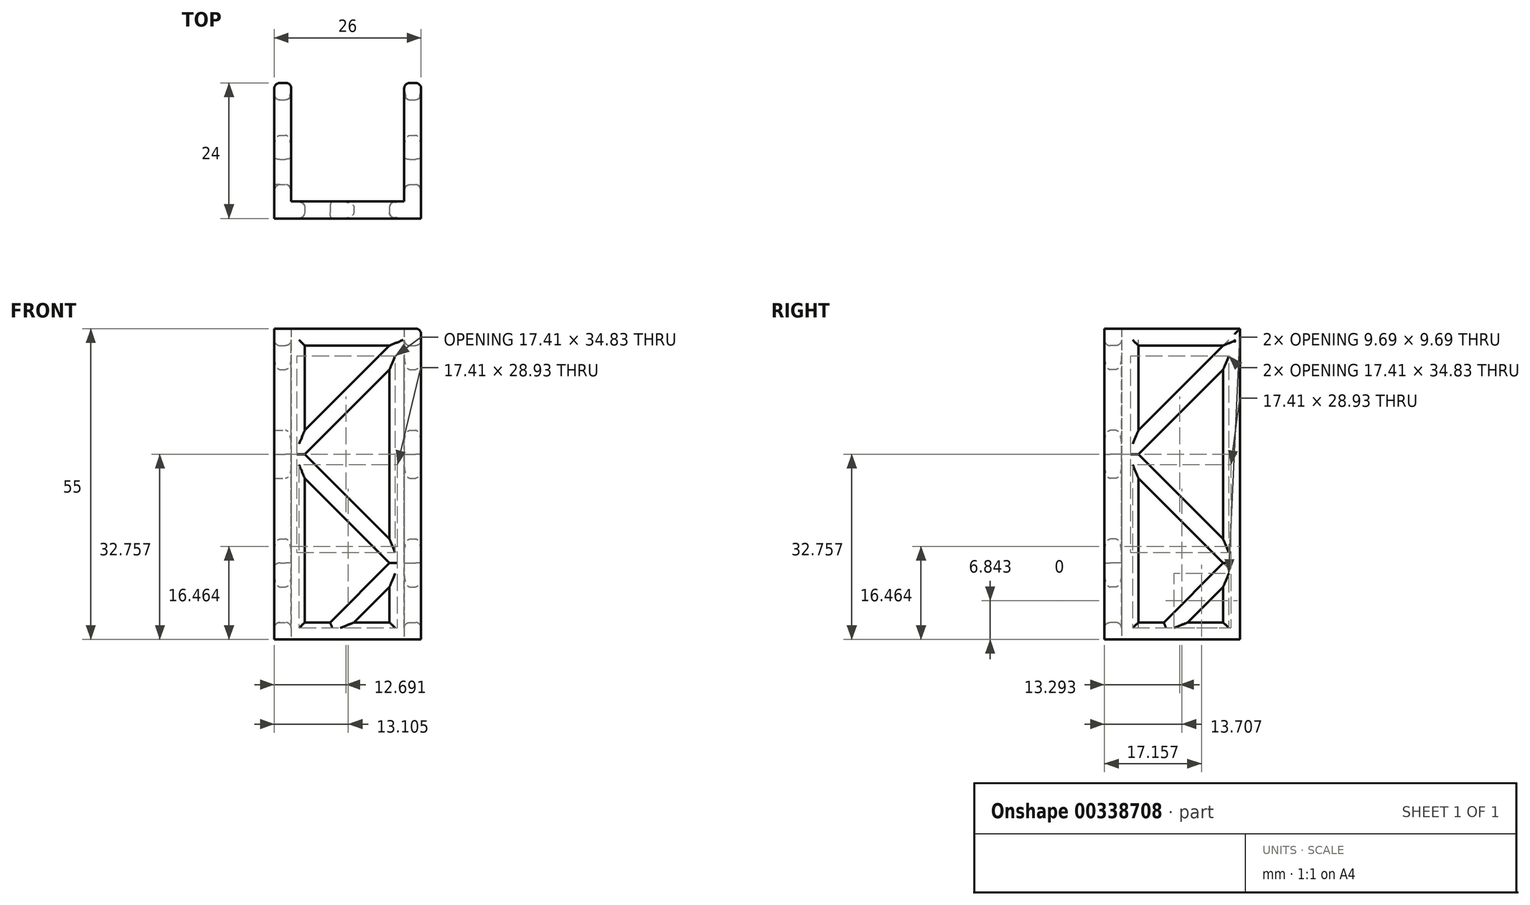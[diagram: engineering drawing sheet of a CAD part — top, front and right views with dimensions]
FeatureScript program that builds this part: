
annotation { "Feature Type Name" : "Feature", "Feature Type Description" : "" }
export const myFeature = defineFeature(function(context is Context, id is Id, definition is map)
    precondition{}
    {
        {
            var Q0;
            Q0=qCreatedBy(makeId("Top.planeOp"),FACE);
            var sketch = newSketch(context, id + "F0", { "sketchPlane" : qUnion([Q0])});
            skLineSegment(sketch, "E0.bottom", {"start": v(-13, 0) * mm, "end": v(-10, 0) * mm});
            skLineSegment(sketch, "E0.top", {"start": v(-13, -24) * mm, "end": v(13, -24) * mm});
            skLineSegment(sketch, "E0.left", {"start": v(-13, 0) * mm, "end": v(-13, -24) * mm});
            skLineSegment(sketch, "E0.right", {"start": v(13, 0) * mm, "end": v(13, -24) * mm});
            skLineSegment(sketch, "E1.top", {"start": v(-10, -21) * mm, "end": v(10, -21) * mm});
            skLineSegment(sketch, "E1.left", {"start": v(-10, 0) * mm, "end": v(-10, -21) * mm});
            skLineSegment(sketch, "E1.right", {"start": v(10, 0) * mm, "end": v(10, -21) * mm});
            skLineSegment(sketch, "E2.trimOffspring", {"start": v(10, 0) * mm, "end": v(13, 0) * mm});
            skSolve(sketch);
        }
        {
            var Q0;
            Q0 = qSketchRegion(id + "F0", true);
            extrude(context, id + "F1", {"entities" : qUnion([Q0]), "endBound" : BoundingType.SYMMETRIC, "depth" : 55 * mm});
        }
        {
            var Q0;
            Q0=makeQuery(id+"F1.opExtrude","SWEPT_FACE",FACE,{"disambiguationData":[OSD([sQuery(id+"F0.wireOp",EDGE,"E0.right")])]});
            var sketch = newSketch(context, id + "F2", { "sketchPlane" : qUnion([Q0])});
            skLineSegment(sketch, "E3", {"start": v(-3, -24.5) * mm, "end": v(-3, 24.5) * mm});
            skLineSegment(sketch, "E4", {"start": v(-18, -24.5) * mm, "end": v(-18, 24.5) * mm});
            skLineSegment(sketch, "E5", {"start": v(-18, 24.5) * mm, "end": v(-3, 24.5) * mm});
            skLineSegment(sketch, "E6", {"start": v(-3, 24.5) * mm, "end": v(-18, 9.5) * mm});
            skLineSegment(sketch, "E7", {"start": v(-3, 20.26) * mm, "end": v(-18, 5.26) * mm});
            skLineSegment(sketch, "E8", {"start": v(-18, 5.26) * mm, "end": v(-3, -9.74) * mm});
            skLineSegment(sketch, "E9.0", {"start": v(-18, 1.01) * mm, "end": v(-3, -13.99) * mm});
            skLineSegment(sketch, "E10", {"start": v(-18, -24.5) * mm, "end": v(-3, -24.5) * mm});
            skLineSegment(sketch, "E11", {"start": v(-3, -13.99) * mm, "end": v(-13.51, -24.5) * mm});
            skLineSegment(sketch, "E12.0", {"start": v(-3, -18.23) * mm, "end": v(-9.27, -24.5) * mm});
            skPoint(sketch, "E13.start.orphan", {"position": v(0, 47.5) * mm});
            skSolve(sketch);
        }
        {
            var Q0;
            {var subQ0=sQuery(id+"F2.wireOp",EDGE,"E5");Q0=makeQuery(id+"F2.imprint","IMPRINT",FACE,{"disambiguationData":[TD([[makeQuery(id+"F2.imprint","IMPRINT",EDGE,{"derivedFrom":subQ0}),-1.0]])]});}
            var Q1;
            {var subQ0=sQuery(id+"F2.wireOp",EDGE,"E7");Q1=makeQuery(id+"F2.imprint","IMPRINT",FACE,{"disambiguationData":[TD([[makeQuery(id+"F2.imprint","IMPRINT",EDGE,{"derivedFrom":subQ0}),1.0]])]});}
            var Q2;
            {var subQ3=sQuery(id+"F2.wireOp",EDGE,"E9.0");Q2=makeQuery(id+"F2.imprint","IMPRINT",FACE,{"disambiguationData":[TD([[makeQuery(id+"F2.imprint","IMPRINT",EDGE,{"derivedFrom":subQ3}),-1.0]])]});}
            var Q3;
            {var subQ3=sQuery(id+"F2.wireOp",EDGE,"E12.0");Q3=makeQuery(id+"F2.imprint","IMPRINT",FACE,{"disambiguationData":[TD([[makeQuery(id+"F2.imprint","IMPRINT",EDGE,{"derivedFrom":subQ3}),1.0]])]});}
            extrude(context, id + "F3", {"entities" : qUnion([Q0, Q1, Q2, Q3]), "operationType" : NewBodyOperationType.REMOVE, "endBound" : BoundingType.SYMMETRIC, "oppositeDirection" : true, "depth" : 1000 * mm});
        }
        {
            var Q0;
            Q0=qCreatedBy(makeId("Front.planeOp"),FACE);
            var sketch = newSketch(context, id + "F4", { "sketchPlane" : qUnion([Q0])});
            skLineSegment(sketch, "E14", {"start": v(7.4, -24.5) * mm, "end": v(7.4, 24.5) * mm});
            skLineSegment(sketch, "E15", {"start": v(-7.6, -24.5) * mm, "end": v(-7.6, 24.5) * mm});
            skLineSegment(sketch, "E16", {"start": v(-7.6, 24.5) * mm, "end": v(7.4, 24.5) * mm});
            skLineSegment(sketch, "E17", {"start": v(7.4, 24.5) * mm, "end": v(-7.6, 9.5) * mm});
            skLineSegment(sketch, "E18", {"start": v(7.4, 20.26) * mm, "end": v(-7.6, 5.26) * mm});
            skLineSegment(sketch, "E19", {"start": v(-7.6, 5.26) * mm, "end": v(7.4, -9.74) * mm});
            skLineSegment(sketch, "E20.0", {"start": v(-7.6, 1.01) * mm, "end": v(7.4, -13.99) * mm});
            skLineSegment(sketch, "E21", {"start": v(-7.6, -24.5) * mm, "end": v(7.4, -24.5) * mm});
            skLineSegment(sketch, "E22", {"start": v(7.4, -13.99) * mm, "end": v(-3.12, -24.5) * mm});
            skLineSegment(sketch, "E23.0", {"start": v(7.4, -18.23) * mm, "end": v(1.13, -24.5) * mm});
            skSolve(sketch);
        }
        {
            var Q0;
            {var subQ3=sQuery(id+"F4.wireOp",EDGE,"E23.0");Q0=makeQuery(id+"F4.imprint","IMPRINT",FACE,{"disambiguationData":[TD([[makeQuery(id+"F4.imprint","IMPRINT",EDGE,{"derivedFrom":subQ3}),1.0]])]});}
            var Q1;
            {var subQ3=sQuery(id+"F4.wireOp",EDGE,"E20.0");Q1=makeQuery(id+"F4.imprint","IMPRINT",FACE,{"disambiguationData":[TD([[makeQuery(id+"F4.imprint","IMPRINT",EDGE,{"derivedFrom":subQ3}),-1.0]])]});}
            var Q2;
            {var subQ0=sQuery(id+"F4.wireOp",EDGE,"E18");Q2=makeQuery(id+"F4.imprint","IMPRINT",FACE,{"disambiguationData":[TD([[makeQuery(id+"F4.imprint","IMPRINT",EDGE,{"derivedFrom":subQ0}),1.0]])]});}
            var Q3;
            {var subQ0=sQuery(id+"F4.wireOp",EDGE,"E16");Q3=makeQuery(id+"F4.imprint","IMPRINT",FACE,{"disambiguationData":[TD([[makeQuery(id+"F4.imprint","IMPRINT",EDGE,{"derivedFrom":subQ0}),-1.0]])]});}
            extrude(context, id + "F5", {"entities" : qUnion([Q0, Q1, Q2, Q3]), "operationType" : NewBodyOperationType.REMOVE, "endBound" : BoundingType.SYMMETRIC, "oppositeDirection" : true, "depth" : 1000 * mm});
        }
        {
            var Q0;
            Q0=makeQuery(id+"F1.opExtrude","SWEPT_EDGE",EDGE,{"disambiguationData":[OSD([sQuery(id+"F0.wireOp",EDGE,"E1.right"),sQuery(id+"F0.wireOp",EDGE,"E2.trimOffspring")])]});
            var Q1;
            Q1=makeQuery(id+"F3.boolean.opBoolean","INTERSECT",EDGE,{"derivedFrom":[makeQuery(id+"F1.opExtrude","SWEPT_FACE",FACE,{"disambiguationData":[OSD([sQuery(id+"F0.wireOp",EDGE,"E0.right")])]}),makeQuery(id+"F3.opExtrude","SWEPT_FACE",FACE,{"disambiguationData":[OSD([sQuery(id+"F2.wireOp",EDGE,"E7")])]})]});
            var Q2;
            {var subQ0=sQuery(id+"F2.wireOp",EDGE,"E3");Q2=makeQuery(id+"F3.boolean.opBoolean","INTERSECT",EDGE,{"derivedFrom":[makeQuery(id+"F1.opExtrude","SWEPT_FACE",FACE,{"disambiguationData":[OSD([sQuery(id+"F0.wireOp",EDGE,"E0.right")])]}),makeQuery(id+"F3.opExtrude","SWEPT_FACE",FACE,{"disambiguationData":[OSD([subQ0]),TDD([makeQuery(id+"F2.imprint","IMPRINT",EDGE,{"disambiguationData":[TD([[makeQuery(id+"F2.imprint","INTERSECT",VERTEX,{"derivedFrom":[subQ0,sQuery(id+"F2.wireOp",EDGE,"E7")]}),1.0]])],"derivedFrom":subQ0})])]})]});}
            var Q3;
            Q3=makeQuery(id+"F3.boolean.opBoolean","INTERSECT",EDGE,{"derivedFrom":[makeQuery(id+"F1.opExtrude","SWEPT_FACE",FACE,{"disambiguationData":[OSD([sQuery(id+"F0.wireOp",EDGE,"E0.right")])]}),makeQuery(id+"F3.opExtrude","SWEPT_FACE",FACE,{"disambiguationData":[OSD([sQuery(id+"F2.wireOp",EDGE,"E8")])]})]});
            var Q4;
            Q4=makeQuery(id+"F3.boolean.opBoolean","INTERSECT",EDGE,{"derivedFrom":[makeQuery(id+"F1.opExtrude","SWEPT_FACE",FACE,{"disambiguationData":[OSD([sQuery(id+"F0.wireOp",EDGE,"E0.right")])]}),makeQuery(id+"F3.opExtrude","SWEPT_FACE",FACE,{"disambiguationData":[OSD([sQuery(id+"F2.wireOp",EDGE,"E6")])]})]});
            var Q5;
            {var subQ0=sQuery(id+"F2.wireOp",EDGE,"E4");Q5=makeQuery(id+"F3.boolean.opBoolean","INTERSECT",EDGE,{"derivedFrom":[makeQuery(id+"F1.opExtrude","SWEPT_FACE",FACE,{"disambiguationData":[OSD([sQuery(id+"F0.wireOp",EDGE,"E0.right")])]}),makeQuery(id+"F3.opExtrude","SWEPT_FACE",FACE,{"disambiguationData":[OSD([subQ0]),TDD([makeQuery(id+"F2.imprint","IMPRINT",EDGE,{"disambiguationData":[TD([[makeQuery(id+"F2.imprint","INTERSECT",VERTEX,{"derivedFrom":[subQ0,sQuery(id+"F2.wireOp",EDGE,"E5")]}),1.0]])],"derivedFrom":subQ0})])]})]});}
            var Q6;
            Q6=makeQuery(id+"F3.boolean.opBoolean","INTERSECT",EDGE,{"derivedFrom":[makeQuery(id+"F1.opExtrude","SWEPT_FACE",FACE,{"disambiguationData":[OSD([sQuery(id+"F0.wireOp",EDGE,"E0.right")])]}),makeQuery(id+"F3.opExtrude","SWEPT_FACE",FACE,{"disambiguationData":[OSD([sQuery(id+"F2.wireOp",EDGE,"E5")])]})]});
            var Q7;
            Q7=makeQuery(id+"F3.boolean.opBoolean","INTERSECT",EDGE,{"derivedFrom":[makeQuery(id+"F1.opExtrude","SWEPT_FACE",FACE,{"disambiguationData":[OSD([sQuery(id+"F0.wireOp",EDGE,"E0.right")])]}),makeQuery(id+"F3.opExtrude","SWEPT_FACE",FACE,{"disambiguationData":[OSD([sQuery(id+"F2.wireOp",EDGE,"E9.0")])]})]});
            var Q8;
            {var subQ0=sQuery(id+"F2.wireOp",EDGE,"E4");Q8=makeQuery(id+"F3.boolean.opBoolean","INTERSECT",EDGE,{"derivedFrom":[makeQuery(id+"F1.opExtrude","SWEPT_FACE",FACE,{"disambiguationData":[OSD([sQuery(id+"F0.wireOp",EDGE,"E0.right")])]}),makeQuery(id+"F3.opExtrude","SWEPT_FACE",FACE,{"disambiguationData":[OSD([subQ0]),TDD([makeQuery(id+"F2.imprint","IMPRINT",EDGE,{"disambiguationData":[TD([[makeQuery(id+"F2.imprint","INTERSECT",VERTEX,{"derivedFrom":[subQ0,sQuery(id+"F2.wireOp",EDGE,"E10")]}),-1.0]])],"derivedFrom":subQ0})])]})]});}
            var Q9;
            {var subQ0=sQuery(id+"F2.wireOp",EDGE,"E10");Q9=makeQuery(id+"F3.boolean.opBoolean","INTERSECT",EDGE,{"derivedFrom":[makeQuery(id+"F1.opExtrude","SWEPT_FACE",FACE,{"disambiguationData":[OSD([sQuery(id+"F0.wireOp",EDGE,"E0.right")])]}),makeQuery(id+"F3.opExtrude","SWEPT_FACE",FACE,{"disambiguationData":[OSD([subQ0]),TDD([makeQuery(id+"F2.imprint","IMPRINT",EDGE,{"disambiguationData":[TD([[makeQuery(id+"F2.imprint","INTERSECT",VERTEX,{"derivedFrom":[sQuery(id+"F2.wireOp",EDGE,"E4"),subQ0]}),-1.0]])],"derivedFrom":subQ0})])]})]});}
            var Q10;
            Q10=makeQuery(id+"F3.boolean.opBoolean","INTERSECT",EDGE,{"derivedFrom":[makeQuery(id+"F1.opExtrude","SWEPT_FACE",FACE,{"disambiguationData":[OSD([sQuery(id+"F0.wireOp",EDGE,"E0.right")])]}),makeQuery(id+"F3.opExtrude","SWEPT_FACE",FACE,{"disambiguationData":[OSD([sQuery(id+"F2.wireOp",EDGE,"E11")])]})]});
            var Q11;
            Q11=makeQuery(id+"F3.boolean.opBoolean","INTERSECT",EDGE,{"derivedFrom":[makeQuery(id+"F1.opExtrude","SWEPT_FACE",FACE,{"disambiguationData":[OSD([sQuery(id+"F0.wireOp",EDGE,"E1.left")])]}),makeQuery(id+"F3.opExtrude","SWEPT_FACE",FACE,{"disambiguationData":[OSD([sQuery(id+"F2.wireOp",EDGE,"E8")])]})]});
            var Q12;
            Q12=makeQuery(id+"F3.boolean.opBoolean","INTERSECT",EDGE,{"derivedFrom":[makeQuery(id+"F1.opExtrude","SWEPT_FACE",FACE,{"disambiguationData":[OSD([sQuery(id+"F0.wireOp",EDGE,"E1.left")])]}),makeQuery(id+"F3.opExtrude","SWEPT_FACE",FACE,{"disambiguationData":[OSD([sQuery(id+"F2.wireOp",EDGE,"E7")])]})]});
            var Q13;
            {var subQ0=sQuery(id+"F2.wireOp",EDGE,"E4");Q13=makeQuery(id+"F3.boolean.opBoolean","INTERSECT",EDGE,{"derivedFrom":[makeQuery(id+"F1.opExtrude","SWEPT_FACE",FACE,{"disambiguationData":[OSD([sQuery(id+"F0.wireOp",EDGE,"E1.left")])]}),makeQuery(id+"F3.opExtrude","SWEPT_FACE",FACE,{"disambiguationData":[OSD([subQ0]),TDD([makeQuery(id+"F2.imprint","IMPRINT",EDGE,{"disambiguationData":[TD([[makeQuery(id+"F2.imprint","INTERSECT",VERTEX,{"derivedFrom":[subQ0,sQuery(id+"F2.wireOp",EDGE,"E5")]}),1.0]])],"derivedFrom":subQ0})])]})]});}
            var Q14;
            Q14=makeQuery(id+"F3.boolean.opBoolean","INTERSECT",EDGE,{"derivedFrom":[makeQuery(id+"F1.opExtrude","SWEPT_FACE",FACE,{"disambiguationData":[OSD([sQuery(id+"F0.wireOp",EDGE,"E1.left")])]}),makeQuery(id+"F3.opExtrude","SWEPT_FACE",FACE,{"disambiguationData":[OSD([sQuery(id+"F2.wireOp",EDGE,"E6")])]})]});
            var Q15;
            Q15=makeQuery(id+"F3.boolean.opBoolean","INTERSECT",EDGE,{"derivedFrom":[makeQuery(id+"F1.opExtrude","SWEPT_FACE",FACE,{"disambiguationData":[OSD([sQuery(id+"F0.wireOp",EDGE,"E1.left")])]}),makeQuery(id+"F3.opExtrude","SWEPT_FACE",FACE,{"disambiguationData":[OSD([sQuery(id+"F2.wireOp",EDGE,"E5")])]})]});
            var Q16;
            {var subQ0=sQuery(id+"F2.wireOp",EDGE,"E3");Q16=makeQuery(id+"F3.boolean.opBoolean","INTERSECT",EDGE,{"derivedFrom":[makeQuery(id+"F1.opExtrude","SWEPT_FACE",FACE,{"disambiguationData":[OSD([sQuery(id+"F0.wireOp",EDGE,"E1.left")])]}),makeQuery(id+"F3.opExtrude","SWEPT_FACE",FACE,{"disambiguationData":[OSD([subQ0]),TDD([makeQuery(id+"F2.imprint","IMPRINT",EDGE,{"disambiguationData":[TD([[makeQuery(id+"F2.imprint","INTERSECT",VERTEX,{"derivedFrom":[subQ0,sQuery(id+"F2.wireOp",EDGE,"E7")]}),1.0]])],"derivedFrom":subQ0})])]})]});}
            var Q17;
            Q17=makeQuery(id+"F1.opExtrude","SWEPT_EDGE",EDGE,{"disambiguationData":[OSD([sQuery(id+"F0.wireOp",EDGE,"E0.bottom"),sQuery(id+"F0.wireOp",EDGE,"E1.left")])]});
            var Q18;
            Q18=makeQuery(id+"F1.opExtrude","SWEPT_EDGE",EDGE,{"disambiguationData":[OSD([sQuery(id+"F0.wireOp",EDGE,"E0.bottom"),sQuery(id+"F0.wireOp",EDGE,"E0.left")])]});
            var Q19;
            Q19=makeQuery(id+"F1.opExtrude","CAP_EDGE",EDGE,{"disambiguationData":[OSD([sQuery(id+"F0.wireOp",EDGE,"E0.right")])],"isStart":false});
            var Q20;
            Q20=makeQuery(id+"F3.boolean.opBoolean","INTERSECT",EDGE,{"derivedFrom":[makeQuery(id+"F1.opExtrude","SWEPT_FACE",FACE,{"disambiguationData":[OSD([sQuery(id+"F0.wireOp",EDGE,"E0.right")])]}),makeQuery(id+"F3.opExtrude","SWEPT_FACE",FACE,{"disambiguationData":[OSD([sQuery(id+"F2.wireOp",EDGE,"E12.0")])]})]});
            var Q21;
            {var subQ0=sQuery(id+"F2.wireOp",EDGE,"E3");Q21=makeQuery(id+"F3.boolean.opBoolean","INTERSECT",EDGE,{"derivedFrom":[makeQuery(id+"F1.opExtrude","SWEPT_FACE",FACE,{"disambiguationData":[OSD([sQuery(id+"F0.wireOp",EDGE,"E0.right")])]}),makeQuery(id+"F3.opExtrude","SWEPT_FACE",FACE,{"disambiguationData":[OSD([subQ0]),TDD([makeQuery(id+"F2.imprint","IMPRINT",EDGE,{"disambiguationData":[TD([[makeQuery(id+"F2.imprint","INTERSECT",VERTEX,{"derivedFrom":[subQ0,sQuery(id+"F2.wireOp",EDGE,"E10")]}),-1.0]])],"derivedFrom":subQ0})])]})]});}
            var Q22;
            {var subQ0=sQuery(id+"F2.wireOp",EDGE,"E10");Q22=makeQuery(id+"F3.boolean.opBoolean","INTERSECT",EDGE,{"derivedFrom":[makeQuery(id+"F1.opExtrude","SWEPT_FACE",FACE,{"disambiguationData":[OSD([sQuery(id+"F0.wireOp",EDGE,"E0.right")])]}),makeQuery(id+"F3.opExtrude","SWEPT_FACE",FACE,{"disambiguationData":[OSD([subQ0]),TDD([makeQuery(id+"F2.imprint","IMPRINT",EDGE,{"disambiguationData":[TD([[makeQuery(id+"F2.imprint","INTERSECT",VERTEX,{"derivedFrom":[sQuery(id+"F2.wireOp",EDGE,"E3"),subQ0]}),1.0]])],"derivedFrom":subQ0})])]})]});}
            var Q23;
            Q23=makeQuery(id+"F1.opExtrude","SWEPT_EDGE",EDGE,{"disambiguationData":[OSD([sQuery(id+"F0.wireOp",EDGE,"E0.right"),sQuery(id+"F0.wireOp",EDGE,"E2.trimOffspring")])]});
            var Q24;
            Q24=makeQuery(id+"F3.boolean.opBoolean","INTERSECT",EDGE,{"derivedFrom":[makeQuery(id+"F1.opExtrude","SWEPT_FACE",FACE,{"disambiguationData":[OSD([sQuery(id+"F0.wireOp",EDGE,"E1.right")])]}),makeQuery(id+"F3.opExtrude","SWEPT_FACE",FACE,{"disambiguationData":[OSD([sQuery(id+"F2.wireOp",EDGE,"E5")])]})]});
            var Q25;
            {var subQ0=sQuery(id+"F2.wireOp",EDGE,"E4");Q25=makeQuery(id+"F3.boolean.opBoolean","INTERSECT",EDGE,{"derivedFrom":[makeQuery(id+"F1.opExtrude","SWEPT_FACE",FACE,{"disambiguationData":[OSD([sQuery(id+"F0.wireOp",EDGE,"E1.right")])]}),makeQuery(id+"F3.opExtrude","SWEPT_FACE",FACE,{"disambiguationData":[OSD([subQ0]),TDD([makeQuery(id+"F2.imprint","IMPRINT",EDGE,{"disambiguationData":[TD([[makeQuery(id+"F2.imprint","INTERSECT",VERTEX,{"derivedFrom":[subQ0,sQuery(id+"F2.wireOp",EDGE,"E5")]}),1.0]])],"derivedFrom":subQ0})])]})]});}
            var Q26;
            Q26=makeQuery(id+"F3.boolean.opBoolean","INTERSECT",EDGE,{"derivedFrom":[makeQuery(id+"F1.opExtrude","SWEPT_FACE",FACE,{"disambiguationData":[OSD([sQuery(id+"F0.wireOp",EDGE,"E1.right")])]}),makeQuery(id+"F3.opExtrude","SWEPT_FACE",FACE,{"disambiguationData":[OSD([sQuery(id+"F2.wireOp",EDGE,"E6")])]})]});
            var Q27;
            Q27=makeQuery(id+"F3.boolean.opBoolean","INTERSECT",EDGE,{"derivedFrom":[makeQuery(id+"F1.opExtrude","SWEPT_FACE",FACE,{"disambiguationData":[OSD([sQuery(id+"F0.wireOp",EDGE,"E1.right")])]}),makeQuery(id+"F3.opExtrude","SWEPT_FACE",FACE,{"disambiguationData":[OSD([sQuery(id+"F2.wireOp",EDGE,"E7")])]})]});
            var Q28;
            Q28=makeQuery(id+"F3.boolean.opBoolean","INTERSECT",EDGE,{"derivedFrom":[makeQuery(id+"F1.opExtrude","SWEPT_FACE",FACE,{"disambiguationData":[OSD([sQuery(id+"F0.wireOp",EDGE,"E1.right")])]}),makeQuery(id+"F3.opExtrude","SWEPT_FACE",FACE,{"disambiguationData":[OSD([sQuery(id+"F2.wireOp",EDGE,"E8")])]})]});
            var Q29;
            {var subQ0=sQuery(id+"F2.wireOp",EDGE,"E3");Q29=makeQuery(id+"F3.boolean.opBoolean","INTERSECT",EDGE,{"derivedFrom":[makeQuery(id+"F1.opExtrude","SWEPT_FACE",FACE,{"disambiguationData":[OSD([sQuery(id+"F0.wireOp",EDGE,"E1.right")])]}),makeQuery(id+"F3.opExtrude","SWEPT_FACE",FACE,{"disambiguationData":[OSD([subQ0]),TDD([makeQuery(id+"F2.imprint","IMPRINT",EDGE,{"disambiguationData":[TD([[makeQuery(id+"F2.imprint","INTERSECT",VERTEX,{"derivedFrom":[subQ0,sQuery(id+"F2.wireOp",EDGE,"E7")]}),1.0]])],"derivedFrom":subQ0})])]})]});}
            var Q30;
            Q30=makeQuery(id+"F3.boolean.opBoolean","INTERSECT",EDGE,{"derivedFrom":[makeQuery(id+"F1.opExtrude","SWEPT_FACE",FACE,{"disambiguationData":[OSD([sQuery(id+"F0.wireOp",EDGE,"E1.right")])]}),makeQuery(id+"F3.opExtrude","SWEPT_FACE",FACE,{"disambiguationData":[OSD([sQuery(id+"F2.wireOp",EDGE,"E9.0")])]})]});
            var Q31;
            {var subQ0=sQuery(id+"F2.wireOp",EDGE,"E4");Q31=makeQuery(id+"F3.boolean.opBoolean","INTERSECT",EDGE,{"derivedFrom":[makeQuery(id+"F1.opExtrude","SWEPT_FACE",FACE,{"disambiguationData":[OSD([sQuery(id+"F0.wireOp",EDGE,"E1.right")])]}),makeQuery(id+"F3.opExtrude","SWEPT_FACE",FACE,{"disambiguationData":[OSD([subQ0]),TDD([makeQuery(id+"F2.imprint","IMPRINT",EDGE,{"disambiguationData":[TD([[makeQuery(id+"F2.imprint","INTERSECT",VERTEX,{"derivedFrom":[subQ0,sQuery(id+"F2.wireOp",EDGE,"E10")]}),-1.0]])],"derivedFrom":subQ0})])]})]});}
            var Q32;
            {var subQ0=sQuery(id+"F2.wireOp",EDGE,"E10");Q32=makeQuery(id+"F3.boolean.opBoolean","INTERSECT",EDGE,{"derivedFrom":[makeQuery(id+"F1.opExtrude","SWEPT_FACE",FACE,{"disambiguationData":[OSD([sQuery(id+"F0.wireOp",EDGE,"E1.right")])]}),makeQuery(id+"F3.opExtrude","SWEPT_FACE",FACE,{"disambiguationData":[OSD([subQ0]),TDD([makeQuery(id+"F2.imprint","IMPRINT",EDGE,{"disambiguationData":[TD([[makeQuery(id+"F2.imprint","INTERSECT",VERTEX,{"derivedFrom":[sQuery(id+"F2.wireOp",EDGE,"E4"),subQ0]}),-1.0]])],"derivedFrom":subQ0})])]})]});}
            var Q33;
            Q33=makeQuery(id+"F3.boolean.opBoolean","INTERSECT",EDGE,{"derivedFrom":[makeQuery(id+"F1.opExtrude","SWEPT_FACE",FACE,{"disambiguationData":[OSD([sQuery(id+"F0.wireOp",EDGE,"E1.right")])]}),makeQuery(id+"F3.opExtrude","SWEPT_FACE",FACE,{"disambiguationData":[OSD([sQuery(id+"F2.wireOp",EDGE,"E11")])]})]});
            var Q34;
            Q34=makeQuery(id+"F3.boolean.opBoolean","INTERSECT",EDGE,{"derivedFrom":[makeQuery(id+"F1.opExtrude","SWEPT_FACE",FACE,{"disambiguationData":[OSD([sQuery(id+"F0.wireOp",EDGE,"E1.right")])]}),makeQuery(id+"F3.opExtrude","SWEPT_FACE",FACE,{"disambiguationData":[OSD([sQuery(id+"F2.wireOp",EDGE,"E12.0")])]})]});
            var Q35;
            {var subQ0=sQuery(id+"F2.wireOp",EDGE,"E3");Q35=makeQuery(id+"F3.boolean.opBoolean","INTERSECT",EDGE,{"derivedFrom":[makeQuery(id+"F1.opExtrude","SWEPT_FACE",FACE,{"disambiguationData":[OSD([sQuery(id+"F0.wireOp",EDGE,"E1.right")])]}),makeQuery(id+"F3.opExtrude","SWEPT_FACE",FACE,{"disambiguationData":[OSD([subQ0]),TDD([makeQuery(id+"F2.imprint","IMPRINT",EDGE,{"disambiguationData":[TD([[makeQuery(id+"F2.imprint","INTERSECT",VERTEX,{"derivedFrom":[subQ0,sQuery(id+"F2.wireOp",EDGE,"E10")]}),-1.0]])],"derivedFrom":subQ0})])]})]});}
            var Q36;
            {var subQ0=sQuery(id+"F2.wireOp",EDGE,"E10");Q36=makeQuery(id+"F3.boolean.opBoolean","INTERSECT",EDGE,{"derivedFrom":[makeQuery(id+"F1.opExtrude","SWEPT_FACE",FACE,{"disambiguationData":[OSD([sQuery(id+"F0.wireOp",EDGE,"E1.right")])]}),makeQuery(id+"F3.opExtrude","SWEPT_FACE",FACE,{"disambiguationData":[OSD([subQ0]),TDD([makeQuery(id+"F2.imprint","IMPRINT",EDGE,{"disambiguationData":[TD([[makeQuery(id+"F2.imprint","INTERSECT",VERTEX,{"derivedFrom":[sQuery(id+"F2.wireOp",EDGE,"E3"),subQ0]}),1.0]])],"derivedFrom":subQ0})])]})]});}
            var Q37;
            {var subQ0=sQuery(id+"F4.wireOp",EDGE,"E21");Q37=makeQuery(id+"F5.boolean.opBoolean","INTERSECT",EDGE,{"derivedFrom":[makeQuery(id+"F1.opExtrude","SWEPT_FACE",FACE,{"disambiguationData":[OSD([sQuery(id+"F0.wireOp",EDGE,"E1.top")])]}),makeQuery(id+"F5.opExtrude","SWEPT_FACE",FACE,{"disambiguationData":[OSD([subQ0]),TDD([makeQuery(id+"F4.imprint","IMPRINT",EDGE,{"disambiguationData":[TD([[makeQuery(id+"F4.imprint","INTERSECT",VERTEX,{"derivedFrom":[sQuery(id+"F4.wireOp",EDGE,"E14"),subQ0]}),1.0]])],"derivedFrom":subQ0})])]})]});}
            var Q38;
            {var subQ0=sQuery(id+"F4.wireOp",EDGE,"E14");Q38=makeQuery(id+"F5.boolean.opBoolean","INTERSECT",EDGE,{"derivedFrom":[makeQuery(id+"F1.opExtrude","SWEPT_FACE",FACE,{"disambiguationData":[OSD([sQuery(id+"F0.wireOp",EDGE,"E1.top")])]}),makeQuery(id+"F5.opExtrude","SWEPT_FACE",FACE,{"disambiguationData":[OSD([subQ0]),TDD([makeQuery(id+"F4.imprint","IMPRINT",EDGE,{"disambiguationData":[TD([[makeQuery(id+"F4.imprint","INTERSECT",VERTEX,{"derivedFrom":[subQ0,sQuery(id+"F4.wireOp",EDGE,"E21")]}),-1.0]])],"derivedFrom":subQ0})])]})]});}
            var Q39;
            Q39=makeQuery(id+"F5.boolean.opBoolean","INTERSECT",EDGE,{"derivedFrom":[makeQuery(id+"F1.opExtrude","SWEPT_FACE",FACE,{"disambiguationData":[OSD([sQuery(id+"F0.wireOp",EDGE,"E1.top")])]}),makeQuery(id+"F5.opExtrude","SWEPT_FACE",FACE,{"disambiguationData":[OSD([sQuery(id+"F4.wireOp",EDGE,"E23.0")])]})]});
            var Q40;
            Q40=makeQuery(id+"F5.boolean.opBoolean","INTERSECT",EDGE,{"derivedFrom":[makeQuery(id+"F1.opExtrude","SWEPT_FACE",FACE,{"disambiguationData":[OSD([sQuery(id+"F0.wireOp",EDGE,"E1.top")])]}),makeQuery(id+"F5.opExtrude","SWEPT_FACE",FACE,{"disambiguationData":[OSD([sQuery(id+"F4.wireOp",EDGE,"E22")])]})]});
            var Q41;
            Q41=makeQuery(id+"F5.boolean.opBoolean","INTERSECT",EDGE,{"derivedFrom":[makeQuery(id+"F1.opExtrude","SWEPT_FACE",FACE,{"disambiguationData":[OSD([sQuery(id+"F0.wireOp",EDGE,"E1.top")])]}),makeQuery(id+"F5.opExtrude","SWEPT_FACE",FACE,{"disambiguationData":[OSD([sQuery(id+"F4.wireOp",EDGE,"E20.0")])]})]});
            var Q42;
            {var subQ0=sQuery(id+"F4.wireOp",EDGE,"E15");Q42=makeQuery(id+"F5.boolean.opBoolean","INTERSECT",EDGE,{"derivedFrom":[makeQuery(id+"F1.opExtrude","SWEPT_FACE",FACE,{"disambiguationData":[OSD([sQuery(id+"F0.wireOp",EDGE,"E1.top")])]}),makeQuery(id+"F5.opExtrude","SWEPT_FACE",FACE,{"disambiguationData":[OSD([subQ0]),TDD([makeQuery(id+"F4.imprint","IMPRINT",EDGE,{"disambiguationData":[TD([[makeQuery(id+"F4.imprint","INTERSECT",VERTEX,{"derivedFrom":[subQ0,sQuery(id+"F4.wireOp",EDGE,"E21")]}),-1.0]])],"derivedFrom":subQ0})])]})]});}
            var Q43;
            {var subQ0=sQuery(id+"F4.wireOp",EDGE,"E21");Q43=makeQuery(id+"F5.boolean.opBoolean","INTERSECT",EDGE,{"derivedFrom":[makeQuery(id+"F1.opExtrude","SWEPT_FACE",FACE,{"disambiguationData":[OSD([sQuery(id+"F0.wireOp",EDGE,"E1.top")])]}),makeQuery(id+"F5.opExtrude","SWEPT_FACE",FACE,{"disambiguationData":[OSD([subQ0]),TDD([makeQuery(id+"F4.imprint","IMPRINT",EDGE,{"disambiguationData":[TD([[makeQuery(id+"F4.imprint","INTERSECT",VERTEX,{"derivedFrom":[sQuery(id+"F4.wireOp",EDGE,"E15"),subQ0]}),-1.0]])],"derivedFrom":subQ0})])]})]});}
            var Q44;
            Q44=makeQuery(id+"F5.boolean.opBoolean","INTERSECT",EDGE,{"derivedFrom":[makeQuery(id+"F1.opExtrude","SWEPT_FACE",FACE,{"disambiguationData":[OSD([sQuery(id+"F0.wireOp",EDGE,"E1.top")])]}),makeQuery(id+"F5.opExtrude","SWEPT_FACE",FACE,{"disambiguationData":[OSD([sQuery(id+"F4.wireOp",EDGE,"E19")])]})]});
            var Q45;
            Q45=makeQuery(id+"F5.boolean.opBoolean","INTERSECT",EDGE,{"derivedFrom":[makeQuery(id+"F1.opExtrude","SWEPT_FACE",FACE,{"disambiguationData":[OSD([sQuery(id+"F0.wireOp",EDGE,"E1.top")])]}),makeQuery(id+"F5.opExtrude","SWEPT_FACE",FACE,{"disambiguationData":[OSD([sQuery(id+"F4.wireOp",EDGE,"E18")])]})]});
            var Q46;
            {var subQ0=sQuery(id+"F4.wireOp",EDGE,"E14");Q46=makeQuery(id+"F5.boolean.opBoolean","INTERSECT",EDGE,{"derivedFrom":[makeQuery(id+"F1.opExtrude","SWEPT_FACE",FACE,{"disambiguationData":[OSD([sQuery(id+"F0.wireOp",EDGE,"E1.top")])]}),makeQuery(id+"F5.opExtrude","SWEPT_FACE",FACE,{"disambiguationData":[OSD([subQ0]),TDD([makeQuery(id+"F4.imprint","IMPRINT",EDGE,{"disambiguationData":[TD([[makeQuery(id+"F4.imprint","INTERSECT",VERTEX,{"derivedFrom":[subQ0,sQuery(id+"F4.wireOp",EDGE,"E18")]}),1.0]])],"derivedFrom":subQ0})])]})]});}
            var Q47;
            Q47=makeQuery(id+"F5.boolean.opBoolean","INTERSECT",EDGE,{"derivedFrom":[makeQuery(id+"F1.opExtrude","SWEPT_FACE",FACE,{"disambiguationData":[OSD([sQuery(id+"F0.wireOp",EDGE,"E1.top")])]}),makeQuery(id+"F5.opExtrude","SWEPT_FACE",FACE,{"disambiguationData":[OSD([sQuery(id+"F4.wireOp",EDGE,"E17")])]})]});
            var Q48;
            Q48=makeQuery(id+"F5.boolean.opBoolean","INTERSECT",EDGE,{"derivedFrom":[makeQuery(id+"F1.opExtrude","SWEPT_FACE",FACE,{"disambiguationData":[OSD([sQuery(id+"F0.wireOp",EDGE,"E1.top")])]}),makeQuery(id+"F5.opExtrude","SWEPT_FACE",FACE,{"disambiguationData":[OSD([sQuery(id+"F4.wireOp",EDGE,"E16")])]})]});
            var Q49;
            {var subQ0=sQuery(id+"F4.wireOp",EDGE,"E15");Q49=makeQuery(id+"F5.boolean.opBoolean","INTERSECT",EDGE,{"derivedFrom":[makeQuery(id+"F1.opExtrude","SWEPT_FACE",FACE,{"disambiguationData":[OSD([sQuery(id+"F0.wireOp",EDGE,"E1.top")])]}),makeQuery(id+"F5.opExtrude","SWEPT_FACE",FACE,{"disambiguationData":[OSD([subQ0]),TDD([makeQuery(id+"F4.imprint","IMPRINT",EDGE,{"disambiguationData":[TD([[makeQuery(id+"F4.imprint","INTERSECT",VERTEX,{"derivedFrom":[subQ0,sQuery(id+"F4.wireOp",EDGE,"E16")]}),1.0]])],"derivedFrom":subQ0})])]})]});}
            var Q50;
            Q50=makeQuery(id+"F3.boolean.opBoolean","INTERSECT",EDGE,{"derivedFrom":[makeQuery(id+"F1.opExtrude","SWEPT_FACE",FACE,{"disambiguationData":[OSD([sQuery(id+"F0.wireOp",EDGE,"E1.left")])]}),makeQuery(id+"F3.opExtrude","SWEPT_FACE",FACE,{"disambiguationData":[OSD([sQuery(id+"F2.wireOp",EDGE,"E9.0")])]})]});
            var Q51;
            {var subQ0=sQuery(id+"F2.wireOp",EDGE,"E4");Q51=makeQuery(id+"F3.boolean.opBoolean","INTERSECT",EDGE,{"derivedFrom":[makeQuery(id+"F1.opExtrude","SWEPT_FACE",FACE,{"disambiguationData":[OSD([sQuery(id+"F0.wireOp",EDGE,"E1.left")])]}),makeQuery(id+"F3.opExtrude","SWEPT_FACE",FACE,{"disambiguationData":[OSD([subQ0]),TDD([makeQuery(id+"F2.imprint","IMPRINT",EDGE,{"disambiguationData":[TD([[makeQuery(id+"F2.imprint","INTERSECT",VERTEX,{"derivedFrom":[subQ0,sQuery(id+"F2.wireOp",EDGE,"E10")]}),-1.0]])],"derivedFrom":subQ0})])]})]});}
            var Q52;
            {var subQ0=sQuery(id+"F2.wireOp",EDGE,"E10");Q52=makeQuery(id+"F3.boolean.opBoolean","INTERSECT",EDGE,{"derivedFrom":[makeQuery(id+"F1.opExtrude","SWEPT_FACE",FACE,{"disambiguationData":[OSD([sQuery(id+"F0.wireOp",EDGE,"E1.left")])]}),makeQuery(id+"F3.opExtrude","SWEPT_FACE",FACE,{"disambiguationData":[OSD([subQ0]),TDD([makeQuery(id+"F2.imprint","IMPRINT",EDGE,{"disambiguationData":[TD([[makeQuery(id+"F2.imprint","INTERSECT",VERTEX,{"derivedFrom":[sQuery(id+"F2.wireOp",EDGE,"E4"),subQ0]}),-1.0]])],"derivedFrom":subQ0})])]})]});}
            var Q53;
            Q53=makeQuery(id+"F3.boolean.opBoolean","INTERSECT",EDGE,{"derivedFrom":[makeQuery(id+"F1.opExtrude","SWEPT_FACE",FACE,{"disambiguationData":[OSD([sQuery(id+"F0.wireOp",EDGE,"E1.left")])]}),makeQuery(id+"F3.opExtrude","SWEPT_FACE",FACE,{"disambiguationData":[OSD([sQuery(id+"F2.wireOp",EDGE,"E11")])]})]});
            var Q54;
            Q54=makeQuery(id+"F3.boolean.opBoolean","INTERSECT",EDGE,{"derivedFrom":[makeQuery(id+"F1.opExtrude","SWEPT_FACE",FACE,{"disambiguationData":[OSD([sQuery(id+"F0.wireOp",EDGE,"E1.left")])]}),makeQuery(id+"F3.opExtrude","SWEPT_FACE",FACE,{"disambiguationData":[OSD([sQuery(id+"F2.wireOp",EDGE,"E12.0")])]})]});
            var Q55;
            {var subQ0=sQuery(id+"F2.wireOp",EDGE,"E3");Q55=makeQuery(id+"F3.boolean.opBoolean","INTERSECT",EDGE,{"derivedFrom":[makeQuery(id+"F1.opExtrude","SWEPT_FACE",FACE,{"disambiguationData":[OSD([sQuery(id+"F0.wireOp",EDGE,"E1.left")])]}),makeQuery(id+"F3.opExtrude","SWEPT_FACE",FACE,{"disambiguationData":[OSD([subQ0]),TDD([makeQuery(id+"F2.imprint","IMPRINT",EDGE,{"disambiguationData":[TD([[makeQuery(id+"F2.imprint","INTERSECT",VERTEX,{"derivedFrom":[subQ0,sQuery(id+"F2.wireOp",EDGE,"E10")]}),-1.0]])],"derivedFrom":subQ0})])]})]});}
            var Q56;
            {var subQ0=sQuery(id+"F2.wireOp",EDGE,"E10");Q56=makeQuery(id+"F3.boolean.opBoolean","INTERSECT",EDGE,{"derivedFrom":[makeQuery(id+"F1.opExtrude","SWEPT_FACE",FACE,{"disambiguationData":[OSD([sQuery(id+"F0.wireOp",EDGE,"E1.left")])]}),makeQuery(id+"F3.opExtrude","SWEPT_FACE",FACE,{"disambiguationData":[OSD([subQ0]),TDD([makeQuery(id+"F2.imprint","IMPRINT",EDGE,{"disambiguationData":[TD([[makeQuery(id+"F2.imprint","INTERSECT",VERTEX,{"derivedFrom":[sQuery(id+"F2.wireOp",EDGE,"E3"),subQ0]}),1.0]])],"derivedFrom":subQ0})])]})]});}
            fillet(context, id + "F6", {"entities" : qUnion([Q0, Q1, Q2, Q3, Q4, Q5, Q6, Q7, Q8, Q9, Q10, Q11, Q12, Q13, Q14, Q15, Q16, Q17, Q18, Q19, Q20, Q21, Q22, Q23, Q24, Q25, Q26, Q27, Q28, Q29, Q30, Q31, Q32, Q33, Q34, Q35, Q36, Q37, Q38, Q39, Q40, Q41, Q42, Q43, Q44, Q45, Q46, Q47, Q48, Q49, Q50, Q51, Q52, Q53, Q54, Q55, Q56]), "radius" : 1 * mm, "tangentPropagation" : true, "allowEdgeOverflow" : false});
        }
        {
            var Q0;
            Q0=makeQuery(id+"F3.boolean.opBoolean","INTERSECT",EDGE,{"derivedFrom":[makeQuery(id+"F1.opExtrude","SWEPT_FACE",FACE,{"disambiguationData":[OSD([sQuery(id+"F0.wireOp",EDGE,"E0.left")])]}),makeQuery(id+"F3.opExtrude","SWEPT_FACE",FACE,{"disambiguationData":[OSD([sQuery(id+"F2.wireOp",EDGE,"E5")])]})]});
            var Q1;
            Q1=makeQuery(id+"F3.boolean.opBoolean","INTERSECT",EDGE,{"derivedFrom":[makeQuery(id+"F1.opExtrude","SWEPT_FACE",FACE,{"disambiguationData":[OSD([sQuery(id+"F0.wireOp",EDGE,"E0.left")])]}),makeQuery(id+"F3.opExtrude","SWEPT_FACE",FACE,{"disambiguationData":[OSD([sQuery(id+"F2.wireOp",EDGE,"E7")])]})]});
            var Q2;
            {var subQ0=sQuery(id+"F2.wireOp",EDGE,"E3");Q2=makeQuery(id+"F3.boolean.opBoolean","INTERSECT",EDGE,{"derivedFrom":[makeQuery(id+"F1.opExtrude","SWEPT_FACE",FACE,{"disambiguationData":[OSD([sQuery(id+"F0.wireOp",EDGE,"E0.left")])]}),makeQuery(id+"F3.opExtrude","SWEPT_FACE",FACE,{"disambiguationData":[OSD([subQ0]),TDD([makeQuery(id+"F2.imprint","IMPRINT",EDGE,{"disambiguationData":[TD([[makeQuery(id+"F2.imprint","INTERSECT",VERTEX,{"derivedFrom":[subQ0,sQuery(id+"F2.wireOp",EDGE,"E7")]}),1.0]])],"derivedFrom":subQ0})])]})]});}
            var Q3;
            Q3=makeQuery(id+"F3.boolean.opBoolean","INTERSECT",EDGE,{"derivedFrom":[makeQuery(id+"F1.opExtrude","SWEPT_FACE",FACE,{"disambiguationData":[OSD([sQuery(id+"F0.wireOp",EDGE,"E0.left")])]}),makeQuery(id+"F3.opExtrude","SWEPT_FACE",FACE,{"disambiguationData":[OSD([sQuery(id+"F2.wireOp",EDGE,"E8")])]})]});
            var Q4;
            {var subQ1=sQuery(id+"F2.wireOp",EDGE,"E9.0");var subQ2=makeQuery(id+"F1.opExtrude","SWEPT_FACE",FACE,{"disambiguationData":[OSD([sQuery(id+"F0.wireOp",EDGE,"E1.left")])]});var subQ3=makeQuery(id+"F3.opExtrude","SWEPT_FACE",FACE,{"disambiguationData":[OSD([subQ1])]});Q4=makeQuery(id+"F6.opFillet","BLEND_EDGE",EDGE,{"blendedFrom":[makeQuery(id+"F3.boolean.opBoolean","INTERSECT",EDGE,{"derivedFrom":[subQ2,subQ3]}),makeQuery(id+"F3.boolean.opBoolean","COPY",FACE,{"disambiguationData":[TD([makeQuery(id+"F1.opExtrude","SWEPT_FACE",FACE,{"disambiguationData":[OSD([sQuery(id+"F0.wireOp",EDGE,"E0.left")])]})])],"derivedFrom":subQ3})],"blendedInto":[makeQuery(id+"F3.boolean.opBoolean","COPY",FACE,{"disambiguationData":[TD([makeQuery(id+"F1.opExtrude","SWEPT_FACE",FACE,{"disambiguationData":[OSD([sQuery(id+"F0.wireOp",EDGE,"E0.left")])]})])],"derivedFrom":subQ3})]});}
            var Q5;
            {var subQ1=makeQuery(id+"F1.opExtrude","SWEPT_FACE",FACE,{"disambiguationData":[OSD([sQuery(id+"F0.wireOp",EDGE,"E1.left")])]});var subQ2=sQuery(id+"F2.wireOp",EDGE,"E10");var subQ3=sQuery(id+"F2.wireOp",EDGE,"E4");var subQ4=makeQuery(id+"F2.imprint","INTERSECT",VERTEX,{"derivedFrom":[subQ3,subQ2]});var subQ5=makeQuery(id+"F3.opExtrude","SWEPT_FACE",FACE,{"disambiguationData":[OSD([subQ3]),TDD([makeQuery(id+"F2.imprint","IMPRINT",EDGE,{"disambiguationData":[TD([[subQ4,-1.0]])],"derivedFrom":subQ3})])]});Q5=makeQuery(id+"F6.opFillet","BLEND_EDGE",EDGE,{"blendedFrom":[makeQuery(id+"F3.boolean.opBoolean","INTERSECT",EDGE,{"derivedFrom":[subQ1,subQ5]}),makeQuery(id+"F3.boolean.opBoolean","COPY",FACE,{"disambiguationData":[TD([makeQuery(id+"F1.opExtrude","SWEPT_FACE",FACE,{"disambiguationData":[OSD([sQuery(id+"F0.wireOp",EDGE,"E0.left")])]})])],"derivedFrom":subQ5})],"blendedInto":[makeQuery(id+"F3.boolean.opBoolean","COPY",FACE,{"disambiguationData":[TD([makeQuery(id+"F1.opExtrude","SWEPT_FACE",FACE,{"disambiguationData":[OSD([sQuery(id+"F0.wireOp",EDGE,"E0.left")])]})])],"derivedFrom":subQ5})]});}
            var Q6;
            Q6=makeQuery(id+"F3.boolean.opBoolean","INTERSECT",EDGE,{"derivedFrom":[makeQuery(id+"F1.opExtrude","SWEPT_FACE",FACE,{"disambiguationData":[OSD([sQuery(id+"F0.wireOp",EDGE,"E0.left")])]}),makeQuery(id+"F3.opExtrude","SWEPT_FACE",FACE,{"disambiguationData":[OSD([sQuery(id+"F2.wireOp",EDGE,"E11")])]})]});
            var Q7;
            {var subQ0=sQuery(id+"F2.wireOp",EDGE,"E10");Q7=makeQuery(id+"F3.boolean.opBoolean","INTERSECT",EDGE,{"derivedFrom":[makeQuery(id+"F1.opExtrude","SWEPT_FACE",FACE,{"disambiguationData":[OSD([sQuery(id+"F0.wireOp",EDGE,"E0.left")])]}),makeQuery(id+"F3.opExtrude","SWEPT_FACE",FACE,{"disambiguationData":[OSD([subQ0]),TDD([makeQuery(id+"F2.imprint","IMPRINT",EDGE,{"disambiguationData":[TD([[makeQuery(id+"F2.imprint","INTERSECT",VERTEX,{"derivedFrom":[sQuery(id+"F2.wireOp",EDGE,"E4"),subQ0]}),-1.0]])],"derivedFrom":subQ0})])]})]});}
            var Q8;
            {var subQ0=sQuery(id+"F2.wireOp",EDGE,"E10");Q8=makeQuery(id+"F3.boolean.opBoolean","INTERSECT",EDGE,{"derivedFrom":[makeQuery(id+"F1.opExtrude","SWEPT_FACE",FACE,{"disambiguationData":[OSD([sQuery(id+"F0.wireOp",EDGE,"E0.left")])]}),makeQuery(id+"F3.opExtrude","SWEPT_FACE",FACE,{"disambiguationData":[OSD([subQ0]),TDD([makeQuery(id+"F2.imprint","IMPRINT",EDGE,{"disambiguationData":[TD([[makeQuery(id+"F2.imprint","INTERSECT",VERTEX,{"derivedFrom":[sQuery(id+"F2.wireOp",EDGE,"E3"),subQ0]}),1.0]])],"derivedFrom":subQ0})])]})]});}
            var Q9;
            Q9=makeQuery(id+"F3.boolean.opBoolean","INTERSECT",EDGE,{"derivedFrom":[makeQuery(id+"F1.opExtrude","SWEPT_FACE",FACE,{"disambiguationData":[OSD([sQuery(id+"F0.wireOp",EDGE,"E0.left")])]}),makeQuery(id+"F3.opExtrude","SWEPT_FACE",FACE,{"disambiguationData":[OSD([sQuery(id+"F2.wireOp",EDGE,"E12.0")])]})]});
            var Q10;
            {var subQ0=sQuery(id+"F2.wireOp",EDGE,"E3");Q10=makeQuery(id+"F3.boolean.opBoolean","INTERSECT",EDGE,{"derivedFrom":[makeQuery(id+"F1.opExtrude","SWEPT_FACE",FACE,{"disambiguationData":[OSD([sQuery(id+"F0.wireOp",EDGE,"E0.left")])]}),makeQuery(id+"F3.opExtrude","SWEPT_FACE",FACE,{"disambiguationData":[OSD([subQ0]),TDD([makeQuery(id+"F2.imprint","IMPRINT",EDGE,{"disambiguationData":[TD([[makeQuery(id+"F2.imprint","INTERSECT",VERTEX,{"derivedFrom":[subQ0,sQuery(id+"F2.wireOp",EDGE,"E10")]}),-1.0]])],"derivedFrom":subQ0})])]})]});}
            var Q11;
            {var subQ0=sQuery(id+"F4.wireOp",EDGE,"E14");Q11=makeQuery(id+"F5.boolean.opBoolean","INTERSECT",EDGE,{"derivedFrom":[makeQuery(id+"F1.opExtrude","SWEPT_FACE",FACE,{"disambiguationData":[OSD([sQuery(id+"F0.wireOp",EDGE,"E0.top")])]}),makeQuery(id+"F5.opExtrude","SWEPT_FACE",FACE,{"disambiguationData":[OSD([subQ0]),TDD([makeQuery(id+"F4.imprint","IMPRINT",EDGE,{"disambiguationData":[TD([[makeQuery(id+"F4.imprint","INTERSECT",VERTEX,{"derivedFrom":[subQ0,sQuery(id+"F4.wireOp",EDGE,"E21")]}),-1.0]])],"derivedFrom":subQ0})])]})]});}
            var Q12;
            {var subQ0=sQuery(id+"F4.wireOp",EDGE,"E21");Q12=makeQuery(id+"F5.boolean.opBoolean","INTERSECT",EDGE,{"derivedFrom":[makeQuery(id+"F1.opExtrude","SWEPT_FACE",FACE,{"disambiguationData":[OSD([sQuery(id+"F0.wireOp",EDGE,"E0.top")])]}),makeQuery(id+"F5.opExtrude","SWEPT_FACE",FACE,{"disambiguationData":[OSD([subQ0]),TDD([makeQuery(id+"F4.imprint","IMPRINT",EDGE,{"disambiguationData":[TD([[makeQuery(id+"F4.imprint","INTERSECT",VERTEX,{"derivedFrom":[sQuery(id+"F4.wireOp",EDGE,"E14"),subQ0]}),1.0]])],"derivedFrom":subQ0})])]})]});}
            var Q13;
            Q13=makeQuery(id+"F5.boolean.opBoolean","INTERSECT",EDGE,{"derivedFrom":[makeQuery(id+"F1.opExtrude","SWEPT_FACE",FACE,{"disambiguationData":[OSD([sQuery(id+"F0.wireOp",EDGE,"E0.top")])]}),makeQuery(id+"F5.opExtrude","SWEPT_FACE",FACE,{"disambiguationData":[OSD([sQuery(id+"F4.wireOp",EDGE,"E23.0")])]})]});
            var Q14;
            Q14=makeQuery(id+"F5.boolean.opBoolean","INTERSECT",EDGE,{"derivedFrom":[makeQuery(id+"F1.opExtrude","SWEPT_FACE",FACE,{"disambiguationData":[OSD([sQuery(id+"F0.wireOp",EDGE,"E0.top")])]}),makeQuery(id+"F5.opExtrude","SWEPT_FACE",FACE,{"disambiguationData":[OSD([sQuery(id+"F4.wireOp",EDGE,"E22")])]})]});
            var Q15;
            {var subQ0=sQuery(id+"F4.wireOp",EDGE,"E21");Q15=makeQuery(id+"F5.boolean.opBoolean","INTERSECT",EDGE,{"derivedFrom":[makeQuery(id+"F1.opExtrude","SWEPT_FACE",FACE,{"disambiguationData":[OSD([sQuery(id+"F0.wireOp",EDGE,"E0.top")])]}),makeQuery(id+"F5.opExtrude","SWEPT_FACE",FACE,{"disambiguationData":[OSD([subQ0]),TDD([makeQuery(id+"F4.imprint","IMPRINT",EDGE,{"disambiguationData":[TD([[makeQuery(id+"F4.imprint","INTERSECT",VERTEX,{"derivedFrom":[sQuery(id+"F4.wireOp",EDGE,"E15"),subQ0]}),-1.0]])],"derivedFrom":subQ0})])]})]});}
            var Q16;
            Q16=makeQuery(id+"F5.boolean.opBoolean","INTERSECT",EDGE,{"derivedFrom":[makeQuery(id+"F1.opExtrude","SWEPT_FACE",FACE,{"disambiguationData":[OSD([sQuery(id+"F0.wireOp",EDGE,"E0.top")])]}),makeQuery(id+"F5.opExtrude","SWEPT_FACE",FACE,{"disambiguationData":[OSD([sQuery(id+"F4.wireOp",EDGE,"E20.0")])]})]});
            var Q17;
            {var subQ0=sQuery(id+"F4.wireOp",EDGE,"E15");Q17=makeQuery(id+"F5.boolean.opBoolean","INTERSECT",EDGE,{"derivedFrom":[makeQuery(id+"F1.opExtrude","SWEPT_FACE",FACE,{"disambiguationData":[OSD([sQuery(id+"F0.wireOp",EDGE,"E0.top")])]}),makeQuery(id+"F5.opExtrude","SWEPT_FACE",FACE,{"disambiguationData":[OSD([subQ0]),TDD([makeQuery(id+"F4.imprint","IMPRINT",EDGE,{"disambiguationData":[TD([[makeQuery(id+"F4.imprint","INTERSECT",VERTEX,{"derivedFrom":[subQ0,sQuery(id+"F4.wireOp",EDGE,"E21")]}),-1.0]])],"derivedFrom":subQ0})])]})]});}
            var Q18;
            {var subQ0=sQuery(id+"F4.wireOp",EDGE,"E15");Q18=makeQuery(id+"F5.boolean.opBoolean","INTERSECT",EDGE,{"derivedFrom":[makeQuery(id+"F1.opExtrude","SWEPT_FACE",FACE,{"disambiguationData":[OSD([sQuery(id+"F0.wireOp",EDGE,"E0.top")])]}),makeQuery(id+"F5.opExtrude","SWEPT_FACE",FACE,{"disambiguationData":[OSD([subQ0]),TDD([makeQuery(id+"F4.imprint","IMPRINT",EDGE,{"disambiguationData":[TD([[makeQuery(id+"F4.imprint","INTERSECT",VERTEX,{"derivedFrom":[subQ0,sQuery(id+"F4.wireOp",EDGE,"E16")]}),1.0]])],"derivedFrom":subQ0})])]})]});}
            var Q19;
            Q19=makeQuery(id+"F5.boolean.opBoolean","INTERSECT",EDGE,{"derivedFrom":[makeQuery(id+"F1.opExtrude","SWEPT_FACE",FACE,{"disambiguationData":[OSD([sQuery(id+"F0.wireOp",EDGE,"E0.top")])]}),makeQuery(id+"F5.opExtrude","SWEPT_FACE",FACE,{"disambiguationData":[OSD([sQuery(id+"F4.wireOp",EDGE,"E16")])]})]});
            var Q20;
            Q20=makeQuery(id+"F5.boolean.opBoolean","INTERSECT",EDGE,{"derivedFrom":[makeQuery(id+"F1.opExtrude","SWEPT_FACE",FACE,{"disambiguationData":[OSD([sQuery(id+"F0.wireOp",EDGE,"E0.top")])]}),makeQuery(id+"F5.opExtrude","SWEPT_FACE",FACE,{"disambiguationData":[OSD([sQuery(id+"F4.wireOp",EDGE,"E17")])]})]});
            var Q21;
            {var subQ0=sQuery(id+"F4.wireOp",EDGE,"E14");Q21=makeQuery(id+"F5.boolean.opBoolean","INTERSECT",EDGE,{"derivedFrom":[makeQuery(id+"F1.opExtrude","SWEPT_FACE",FACE,{"disambiguationData":[OSD([sQuery(id+"F0.wireOp",EDGE,"E0.top")])]}),makeQuery(id+"F5.opExtrude","SWEPT_FACE",FACE,{"disambiguationData":[OSD([subQ0]),TDD([makeQuery(id+"F4.imprint","IMPRINT",EDGE,{"disambiguationData":[TD([[makeQuery(id+"F4.imprint","INTERSECT",VERTEX,{"derivedFrom":[subQ0,sQuery(id+"F4.wireOp",EDGE,"E18")]}),1.0]])],"derivedFrom":subQ0})])]})]});}
            var Q22;
            Q22=makeQuery(id+"F5.boolean.opBoolean","INTERSECT",EDGE,{"derivedFrom":[makeQuery(id+"F1.opExtrude","SWEPT_FACE",FACE,{"disambiguationData":[OSD([sQuery(id+"F0.wireOp",EDGE,"E0.top")])]}),makeQuery(id+"F5.opExtrude","SWEPT_FACE",FACE,{"disambiguationData":[OSD([sQuery(id+"F4.wireOp",EDGE,"E19")])]})]});
            var Q23;
            Q23=makeQuery(id+"F5.boolean.opBoolean","INTERSECT",EDGE,{"derivedFrom":[makeQuery(id+"F1.opExtrude","SWEPT_FACE",FACE,{"disambiguationData":[OSD([sQuery(id+"F0.wireOp",EDGE,"E0.top")])]}),makeQuery(id+"F5.opExtrude","SWEPT_FACE",FACE,{"disambiguationData":[OSD([sQuery(id+"F4.wireOp",EDGE,"E18")])]})]});
            fillet(context, id + "F7", {"entities" : qUnion([Q0, Q1, Q2, Q3, Q4, Q5, Q6, Q7, Q8, Q9, Q10, Q11, Q12, Q13, Q14, Q15, Q16, Q17, Q18, Q19, Q20, Q21, Q22, Q23]), "radius" : 1 * mm, "tangentPropagation" : true, "allowEdgeOverflow" : false});
        }
    });
